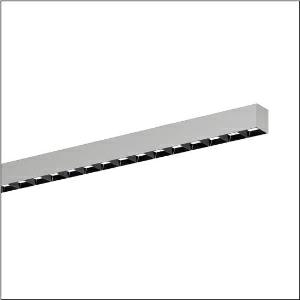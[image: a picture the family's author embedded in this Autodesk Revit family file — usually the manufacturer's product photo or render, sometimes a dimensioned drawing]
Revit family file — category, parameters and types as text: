
# Revit family: silica_r__21_51mx24dc3asb_5aec
name_source: partatom
category: Lighting Fixtures
units: mm (PartAtom-declared; Revit-internal decimal feet)

## family parameters
Cut with Voids When Loaded = No
Host = Face
Light Source = No
Part Type = Normal
Room Calculation Point = No
Round Connector Dimension = Use Diameter
Shared = No

## types (1)
- --- (1 x LED, 10800 lm, 79 W, 3000K)
    Apparent Load = 79 VA
    CIE Flux Codes = 74 94 99 100 100
    Color Rendering = 80
    Color Temperature = 3000K
    Default Elevation = 1800 mm
    Description = Silica® 21, office luminaire, primary light control with darklight reflector, of PMMA, black, CAT 2 (L<= 3000cd/m²), light emission: direct distribution, primary light characteristic: asymmetric, installation type: surface-mounted, LED, rated luminous flux: 10.800lm, luminous efficacy: 137lm/W, light colour: 830, colour temperature: 3000K, with terminal, 3+2-pole, max. 2.5mm², mains connection: 220..240V, AC, 50/60Hz, rated input power: 79W, luminaire housing, of aluminium, metallic grey (RAL 9006), length: 3.004mm, width: 53mm, height: 53mm, protection rating (complete): IP20, insulation class (complete): insulation class I (protective earthing), certification: CE, permissible operating ambient temperature: 0..+35°C, standard: EN 50419, packaging unit: 1 piece
    Height = 0 mm  [stored 0 ft]
    Lamp = 1 x LED
    Lamp Light Flux = 10800 lm
    Lamp Power = 79 W
    Lamp count = 1
    Length = 3004 mm
    Luminous efficacy = 137 lm/W
    Manufacturer = Siteco
    ModVariant = No
    Model = 51MX24DC3ASB
    Mounting Place = Ceiling
    Mounting Type = Recessed
    Number of Poles = 1
    OnlyDefault = Yes
    Power Factor = 1
    Product Name = Silica® 21
    Product group = office luminaire | ceiling recessed
    ProductGroupID = 400
    Protection Class = Protection class I
    Protection Degree = IP 20
    RLX_Detail_Level = 1
    RLX_Emergency_Light_Flux = 0 lm
    RLX_Emergency_Type = 0
    RLX_Emergency_Type_DB = No
    RlxData = <blob elided: 64025 chars, md5=922b13da>
    Socket = socket
    Standby Power = 0 W
    System Light Flux = 10800 lm
    System Power = 79 W
    Type Comments = factory setting: luminous flux: 100 % | dim-lin: 254 | 448 mA
    Type Image = l_1335929.jpg
    URL = http://relux.com
    VarID = @adj_092075
    Voltage = 0 V
    Weight = 0.00 kg
    Width = 53 mm

note: [stored X ft] marks values corroborated as IEEE doubles in the binary element streams (Revit-internal decimal feet)

## geometry (parser evidence)
native form markers: Blend x4, Sweep x10
no freeform markers — native parametric forms only
